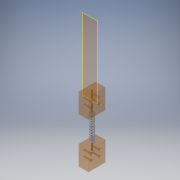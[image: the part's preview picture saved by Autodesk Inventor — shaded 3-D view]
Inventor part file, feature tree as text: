
AUTODESK INVENTOR PART (.ipt)
format: ipt  version: 2016 (Build 200138000, 138)  size: 493,056 bytes
history: native  units: in
note: dims shown in document units (in); Inventor stores cm internally (conversion verified against a paired STEP export)
features: surface_op x3, other x3, reference x2, plane x1, helix x1, sketch x1
ambient origin geometry x8: Origin, YZ Plane, XZ Plane, XY Plane, X Axis, Y Axis, Z Axis, Center Point
bodies: Solid1 (feature_tree)
feature tree (11):
  plane  "Work Plane1"
  helix  "Coil1"  [1 undecoded]
  sketch  "Sketch1"  dims[d1=0.195in d2=2.63in d3=1.0in d4=2.63in d5=7.4803in d6=0.0in d7=90.0deg d8=90.0deg d9=0.0in d10=0.0in]
  reference  "Reference1"
  reference  "Reference2"
  surface_op  "Surface1"
  surface_op  "Surface2"
  surface_op  "Surface3"
  other  "Srf1"
  other  "Srf2"
  other  "Srf3"
note: 1 required parameter value undecoded (feature->parameter linkage not recoverable at this tier; creation-order binding heuristic only, values carry confidence <= 0.55)
